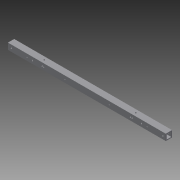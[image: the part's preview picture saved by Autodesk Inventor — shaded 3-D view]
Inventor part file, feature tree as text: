
AUTODESK INVENTOR PART (.ipt)
format: ipt  version: 2015 SP1 (Build 190203100, 203)  size: 155,648 bytes
history: native  units: in
note: dims shown in document units (in); Inventor stores cm internally (conversion verified against a paired STEP export)
features: sketch x6, hole x4, extrude x2
ambient origin geometry x8: Origin, YZ Plane, XZ Plane, XY Plane, X Axis, Y Axis, Z Axis, Center Point
bodies: Solid1 (feature_tree)
feature tree (12):
  extrude  "Extrusion1"  Depth=1.0in
  hole  "Hole1"  [1 undecoded]
  hole  "Hole2"  [1 undecoded]
  hole  "Hole3"  [1 undecoded]
  extrude  "Extrusion2"  Depth=0.5in
  hole  "Hole5"  [1 undecoded]
  sketch  "Sketch1"  dims[d0=1.0in d1=1.0in]
  sketch  "Sketch2"  dims[d2=0.75in d3=0.75in]
  sketch  "Sketch3"  dims[d4=0.125in d5=0.125in]
  sketch  "Sketch4"  dims[d6=25.0in d7=0.0in d8=3.875in]
  sketch  "Sketch6"  dims[d9=1.5in d10=0.5in]
  sketch  "Sketch7"  dims[d11=0.5in d12=0.5in d13=3.875in d14=1.5in d15=0.5in d16=0.25in d17=0.75in d18=0.375in d19=0.25in d20=0.5635in d21=1.0in d22=0.8108in d23=0.5in d24=0.5in d25=0.5in d26=0.5in d27=0.25in d28=0.75in d29=0.375in d30=0.25in d31=0.5635in d32=1.0in d33=0.8108in d34=0.5in d35=0.5in d36=0.5in d37=0.5in d38=3.0in d39=9.0in d40=9.0in d41=3.0in d42=0.1875in d43=0.75in d44=0.375in d45=0.25in d46=0.5635in d47=1.0in d48=0.8108in d61=0.25in d62=0.25in d63=0.25in d64=0.5in d65=0.25in d66=0.5in d67=1.0in d68=0.0in d69=0.5in d70=5.125in d71=0.5in d74=0.1875in d75=0.75in d76=0.375in d77=0.25in d78=0.5635in d79=1.0in d80=0.8108in d81=14.75in]
note: 4 required parameter values undecoded (feature->parameter linkage not recoverable at this tier; creation-order binding heuristic only, values carry confidence <= 0.55)
